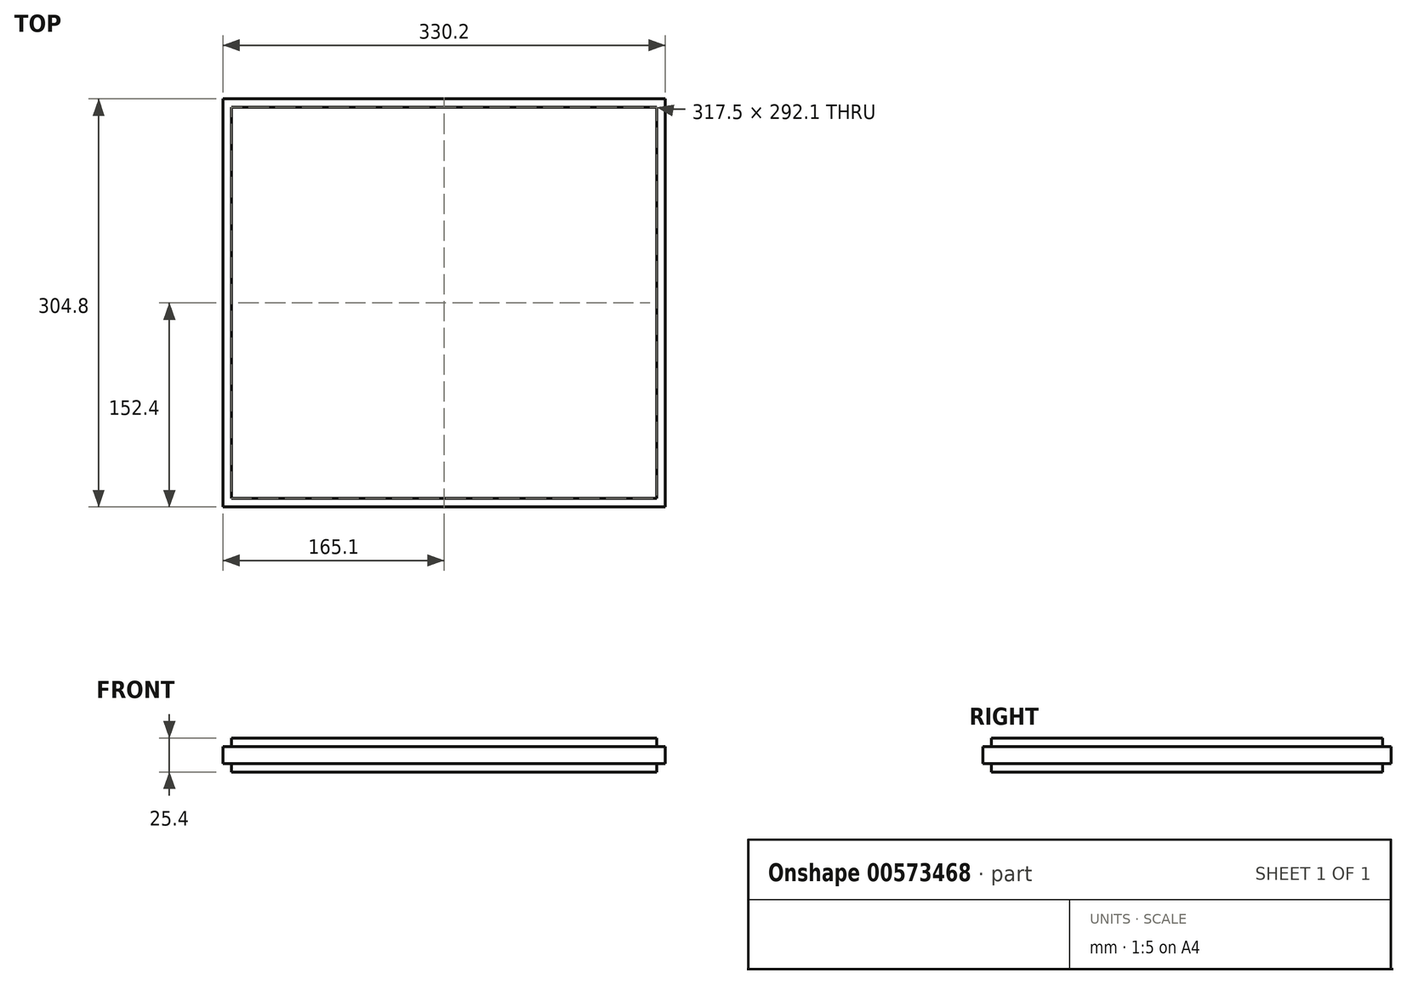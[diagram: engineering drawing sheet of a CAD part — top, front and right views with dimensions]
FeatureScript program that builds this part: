
annotation { "Feature Type Name" : "Feature", "Feature Type Description" : "" }
export const myFeature = defineFeature(function(context is Context, id is Id, definition is map)
    precondition{}
    {
        {
            var Q0;
            Q0=qCreatedBy(makeId("Top.planeOp"),FACE);
            var sketch = newSketch(context, id + "F0", { "sketchPlane" : qUnion([Q0])});
            skLineSegment(sketch, "E0.bottom", {"start": v(158.75, 146.05) * mm, "end": v(-158.75, 146.05) * mm});
            skLineSegment(sketch, "E0.top", {"start": v(158.75, -146.05) * mm, "end": v(-158.75, -146.05) * mm});
            skLineSegment(sketch, "E0.left", {"start": v(158.75, 146.05) * mm, "end": v(158.75, -146.05) * mm});
            skLineSegment(sketch, "E0.right", {"start": v(-158.75, 146.05) * mm, "end": v(-158.75, -146.05) * mm});
            skPoint(sketch, "E0.middle", {"position": v(0, 0) * mm});
            skSolve(sketch);
        }
        {
            var Q0;
            Q0=makeQuery(id+"F0.imprint","IMPRINT",FACE,{"disambiguationData":[TD([[makeQuery(id+"F0.imprint","IMPRINT",EDGE,{"derivedFrom":sQuery(id+"F0.wireOp",EDGE,"E0.bottom")}),1.0]])]});
            extrude(context, id + "F1", {"entities" : qUnion([Q0]), "depth" : 25.4 * mm, "offsetDistance" : 25.4 * mm});
        }
        {
            var Q0;
            Q0=makeQuery(id+"F1.opExtrude","SWEPT_FACE",FACE,{"disambiguationData":[OSD([sQuery(id+"F0.wireOp",EDGE,"E0.left")])]});
            var sketch = newSketch(context, id + "F2", { "sketchPlane" : qUnion([Q0])});
            skLineSegment(sketch, "E1.bottom", {"start": v(-146.05, 0) * mm, "end": v(146.05, 0) * mm});
            skLineSegment(sketch, "E1.top", {"start": v(-146.05, 6.35) * mm, "end": v(146.05, 6.35) * mm});
            skLineSegment(sketch, "E1.left", {"start": v(-146.05, 0) * mm, "end": v(-146.05, 6.35) * mm});
            skLineSegment(sketch, "E1.right", {"start": v(146.05, 0) * mm, "end": v(146.05, 6.35) * mm});
            skLineSegment(sketch, "E2", {"start": v(-146.05, 6.35) * mm, "end": v(-146.05, 19.05) * mm});
            skLineSegment(sketch, "E3", {"start": v(-146.05, 19.05) * mm, "end": v(146.05, 19.05) * mm});
            skLineSegment(sketch, "E4", {"start": v(146.05, 19.05) * mm, "end": v(146.05, 6.35) * mm});
            skSolve(sketch);
        }
        {
            var Q0;
            Q0=makeQuery(id+"F2.imprint","IMPRINT",FACE,{"disambiguationData":[TD([[makeQuery(id+"F2.imprint","IMPRINT",EDGE,{"derivedFrom":sQuery(id+"F2.wireOp",EDGE,"E1.top")}),1.0]])]});
            extrude(context, id + "F3", {"entities" : qUnion([Q0]), "operationType" : NewBodyOperationType.ADD, "depth" : 6.35 * mm, "offsetDistance" : 25.4 * mm});
        }
        {
            var Q0;
            Q0=makeQuery(id+"F1.opExtrude","SWEPT_FACE",FACE,{"disambiguationData":[OSD([sQuery(id+"F0.wireOp",EDGE,"E0.right")])]});
            var sketch = newSketch(context, id + "F4", { "sketchPlane" : qUnion([Q0])});
            skLineSegment(sketch, "E5", {"start": v(-146.05, 0) * mm, "end": v(-146.05, 6.35) * mm});
            skLineSegment(sketch, "E6", {"start": v(-146.05, 19.05) * mm, "end": v(-146.05, 6.35) * mm});
            skLineSegment(sketch, "E7", {"start": v(-146.05, 6.35) * mm, "end": v(146.05, 6.35) * mm});
            skLineSegment(sketch, "E8", {"start": v(146.05, 6.35) * mm, "end": v(146.05, 19.05) * mm});
            skLineSegment(sketch, "E9", {"start": v(146.05, 19.05) * mm, "end": v(-146.05, 19.05) * mm});
            skSolve(sketch);
        }
        {
            var Q0;
            Q0=makeQuery(id+"F4.imprint","IMPRINT",FACE,{"disambiguationData":[TD([[makeQuery(id+"F4.imprint","IMPRINT",EDGE,{"derivedFrom":sQuery(id+"F4.wireOp",EDGE,"E6")}),1.0]])]});
            extrude(context, id + "F5", {"entities" : qUnion([Q0]), "operationType" : NewBodyOperationType.ADD, "depth" : 6.35 * mm, "offsetDistance" : 25.4 * mm});
        }
        {
            var Q0;
            Q0=makeQuery(id+"F5.boolean.opBoolean","MERGE",FACE,{"derivedFrom":[makeQuery(id+"F3.boolean.opBoolean","MERGE",FACE,{"derivedFrom":[makeQuery(id+"F1.opExtrude","SWEPT_FACE",FACE,{"disambiguationData":[OSD([sQuery(id+"F0.wireOp",EDGE,"E0.top")])]}),makeQuery(id+"F3.opExtrude","SWEPT_FACE",FACE,{"disambiguationData":[OSD([sQuery(id+"F2.wireOp",EDGE,"E2")])]})]}),makeQuery(id+"F5.opExtrude","SWEPT_FACE",FACE,{"disambiguationData":[OSD([sQuery(id+"F4.wireOp",EDGE,"E8")])]})]});
            var sketch = newSketch(context, id + "F6", { "sketchPlane" : qUnion([Q0])});
            skLineSegment(sketch, "E10.bottom", {"start": v(-165.1, 19.05) * mm, "end": v(165.1, 19.05) * mm});
            skLineSegment(sketch, "E10.top", {"start": v(-165.1, 6.35) * mm, "end": v(165.1, 6.35) * mm});
            skLineSegment(sketch, "E10.left", {"start": v(-165.1, 19.05) * mm, "end": v(-165.1, 6.35) * mm});
            skLineSegment(sketch, "E10.right", {"start": v(165.1, 19.05) * mm, "end": v(165.1, 6.35) * mm});
            skSolve(sketch);
        }
        {
            var Q0;
            {var subQ15=sQuery(id+"F6.wireOp",EDGE,"E10.left");Q0=makeQuery(id+"F6.imprint","IMPRINT",FACE,{"disambiguationData":[TD([[makeQuery(id+"F6.imprint","IMPRINT",EDGE,{"derivedFrom":subQ15}),1.0]])]});}
            extrude(context, id + "F7", {"entities" : qUnion([Q0]), "operationType" : NewBodyOperationType.ADD, "depth" : 6.35 * mm, "offsetDistance" : 25.4 * mm});
        }
        {
            var Q0;
            Q0=makeQuery(id+"F5.boolean.opBoolean","MERGE",FACE,{"derivedFrom":[makeQuery(id+"F3.boolean.opBoolean","MERGE",FACE,{"derivedFrom":[makeQuery(id+"F1.opExtrude","SWEPT_FACE",FACE,{"disambiguationData":[OSD([sQuery(id+"F0.wireOp",EDGE,"E0.bottom")])]}),makeQuery(id+"F3.opExtrude","SWEPT_FACE",FACE,{"disambiguationData":[OSD([sQuery(id+"F2.wireOp",EDGE,"E4")])]})]}),makeQuery(id+"F5.opExtrude","SWEPT_FACE",FACE,{"disambiguationData":[OSD([sQuery(id+"F4.wireOp",EDGE,"E6")])]})]});
            var sketch = newSketch(context, id + "F8", { "sketchPlane" : qUnion([Q0])});
            skLineSegment(sketch, "E11.bottom", {"start": v(-165.1, 19.05) * mm, "end": v(165.1, 19.05) * mm});
            skLineSegment(sketch, "E11.top", {"start": v(-165.1, 6.35) * mm, "end": v(165.1, 6.35) * mm});
            skLineSegment(sketch, "E11.left", {"start": v(-165.1, 19.05) * mm, "end": v(-165.1, 6.35) * mm});
            skLineSegment(sketch, "E11.right", {"start": v(165.1, 19.05) * mm, "end": v(165.1, 6.35) * mm});
            skSolve(sketch);
        }
        {
            var Q0;
            {var subQ15=sQuery(id+"F8.wireOp",EDGE,"E11.left");Q0=makeQuery(id+"F8.imprint","IMPRINT",FACE,{"disambiguationData":[TD([[makeQuery(id+"F8.imprint","IMPRINT",EDGE,{"derivedFrom":subQ15}),1.0]])]});}
            extrude(context, id + "F9", {"entities" : qUnion([Q0]), "operationType" : NewBodyOperationType.ADD, "depth" : 6.35 * mm, "offsetDistance" : 25.4 * mm});
        }
    });
